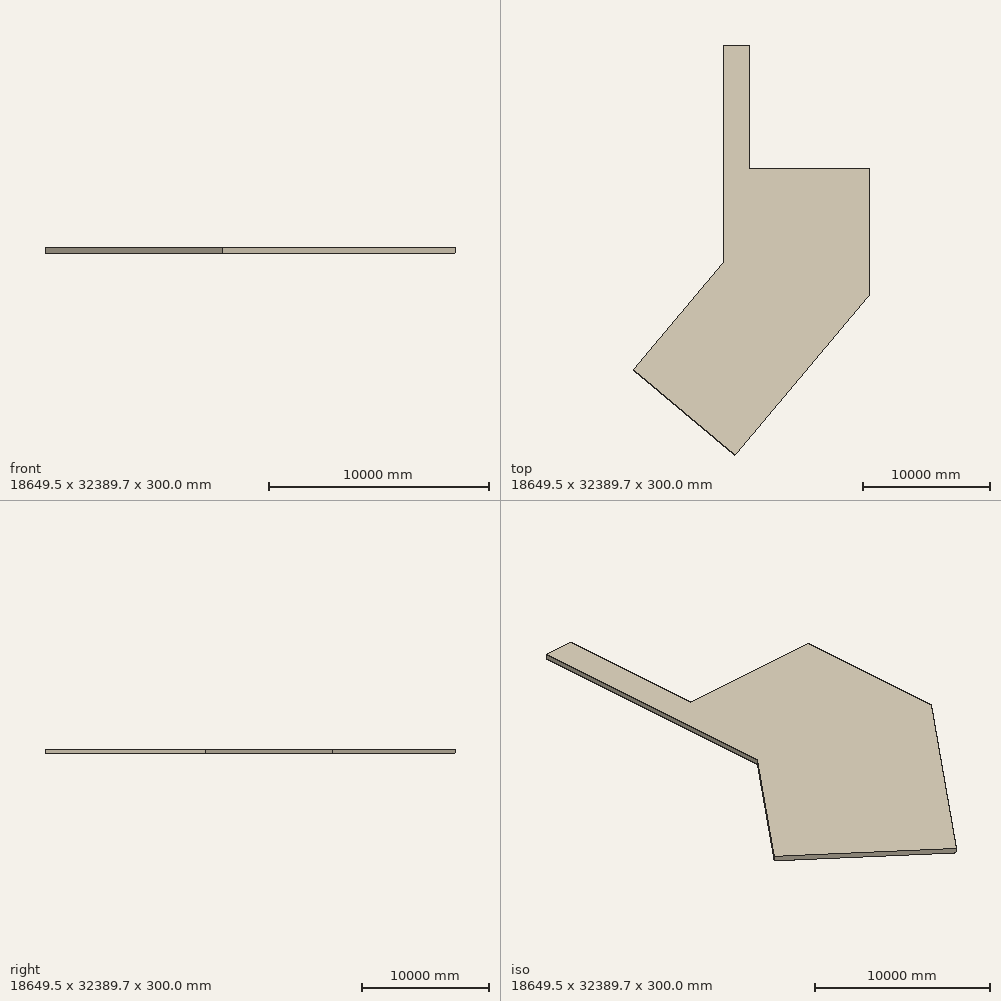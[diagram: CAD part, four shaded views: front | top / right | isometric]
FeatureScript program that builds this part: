
annotation { "Feature Type Name" : "Feature", "Feature Type Description" : "" }
export const myFeature = defineFeature(function(context is Context, id is Id, definition is map)
    precondition{}
    {
        {
            var Q0;
            Q0=qCreatedBy(makeId("Top.planeOp"),FACE);
            var sketch = newSketch(context, id + "F0", { "sketchPlane" : qUnion([Q0])});
            skLineSegment(sketch, "E0", {"start": v(0, 0) * mm, "end": v(0, 9750) * mm});
            skLineSegment(sketch, "E1", {"start": v(0, 9750) * mm, "end": v(-2000, 9750) * mm});
            skLineSegment(sketch, "E2", {"start": v(-2000, 9750) * mm, "end": v(-2000, -7370.07) * mm});
            skLineSegment(sketch, "E3", {"start": v(-2000, -7370.07) * mm, "end": v(-9149.46, -15890.46) * mm});
            skLineSegment(sketch, "E4", {"start": v(-9149.46, -15890.46) * mm, "end": v(-1106, -22639.73) * mm});
            skLineSegment(sketch, "E5", {"start": v(-1106, -22639.73) * mm, "end": v(9500, -10000) * mm});
            skLineSegment(sketch, "E6", {"start": v(9500, -10000) * mm, "end": v(9500, 0) * mm});
            skLineSegment(sketch, "E7", {"start": v(0, 0) * mm, "end": v(9500, 0) * mm});
            skSolve(sketch);
        }
        {
            var Q0;
            Q0 = qSketchRegion(id + "F0", true);
            extrude(context, id + "F1", {"entities" : qUnion([Q0]), "depth" : 300 * mm});
        }
    });
